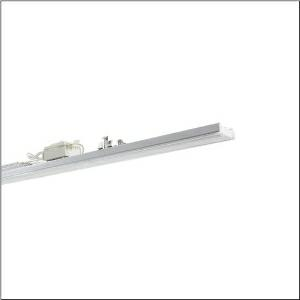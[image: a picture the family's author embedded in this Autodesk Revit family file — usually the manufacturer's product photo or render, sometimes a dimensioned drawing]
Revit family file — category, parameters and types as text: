
# Revit family: licross_11_recessed_mo_51tl1ecn49xg
name_source: partatom
category: Lighting Fixtures
units: mm (PartAtom-declared; Revit-internal decimal feet)

## family parameters
Cut with Voids When Loaded = No
Host = Face
Light Source = No
Part Type = Normal
Room Calculation Point = No
Round Connector Dimension = Use Diameter
Shared = No

## types (1)
- --- (1 x LED, 9000 lm, 49.3 W, 4000K)
    Apparent Load = 49 VA
    CIE Flux Codes = 85 95 99 100 100
    Color Rendering = 80
    Color Temperature = 4000K
    Default Elevation = 1800 mm
    Description = Licross 11 Recessed MO, luminaire insert, of sheet steel, coil coated, white, length: 1.500mm, width: 66mm, height: 67mm, LED rated luminous flux: 9.000lm, light colour: 840, SDCM (Standard Deviation of Colour Matching)MacAdam ≤ 2 SDCM (initial), control gear: ON/OFF Multilumen, CLOi, with plug, 3-pole, with phase selection, mains connection: 220..240V, AC, 50/60Hz, start of lifetime: 49W, end of service life: 55W, internal wiring halogen-free, primary light control with lens, of plastic, primary optical cover: cover, of PMMA, light emission: direct distribution, primary light characteristic: symmetric, protection rating (complete): IP40, insulation class (complete): insulation class I (protective earthing), certification: CE, ENEC, VDE, UKCA, protection symbol: D if used in an environment without relevant dust loads with corresponding accessories, impact resistance: IK06, permissible ambient temperature for indoor applications: -35..+40°C, corresponds to IFS (International Featured Standards) requirements for safety and quality in the food industry, reducing of maximum allowable ambient temperature of 5°C with ceiling mounting, LABS conformity tested according to VDMA 24364:2018-05, The light source and the operating device comply with the requirements of the Ecodesign Regulation (EU) 2019/2020 and are replaceable in accordance with this regulation, packaging unit: 1 piece
    Height = 58 mm
    Lamp = 1 x LED
    Lamp Light Flux = 9000 lm
    Lamp Power = 49.3 W
    Lamp count = 1
    Length = 1500 mm
    Luminous efficacy = 183 lm/W
    Manufacturer = Siteco
    ModVariant = No
    Model = 51TL1ECN49XG
    Mounting Place = Ceiling
    Mounting Type = Pendant
    Number of Poles = 1
    OnlyDefault = Yes
    Power Factor = 1
    Product Name = Licross 11 Recessed MO
    Product group = luminaire insert | ceiling pendant
    ProductGroupID = 901
    Protection Class = Protection class I
    Protection Degree = IP 40
    RLX_Detail_Level = 1
    RLX_Emergency_Light_Flux = 0 lm
    RLX_Emergency_Type = 0
    RLX_Emergency_Type_DB = No
    RlxData = <blob elided: 22721 chars, md5=040bddd2>
    Socket = socket
    Standby Power = 0 W
    System Light Flux = 9000 lm
    System Power = 49 W
    Type Comments = factory setting: luminous flux: 100 % | (A | C | E) | 113 mA
    Type Image = l_1296930.jpg
    URL = http://relux.com
    VarID = @adj_000129
    Voltage = 0 V
    Weight = 0.00 kg
    Width = 66 mm

## geometry (parser evidence)
native form markers: Blend x4, Sweep x11
no freeform markers — native parametric forms only
